# Revit family: Unterflurdose UGD250-3 für GES9_55
name_source: partatom
category: Generic Models
revit_build: Autodesk Revit 2015 (Build: 20140606_1530(x64)
units: mm (PartAtom-declared; Revit-internal decimal feet)

## types (1)
- UGD 250-3 9R
    "A" Dimension = 367 mm  [stored 1.20407 ft]
    "B" Dimension = 367 mm  [stored 1.20407 ft]
    Article Type = UGD55 250-3 9R
    Cover size "a" = 244 mm  [stored 0.800525 ft]
    Cover size "b" = 283 mm  [stored 0.928478 ft]
    GTIN = 4012195678724
    Height = 70 mm  [stored 0.229659 ft]
    HeightCalc = 70 mm  [stored 0.229659 ft]
    Manufacturer = OBO Bettermann
    Manufacturer Art. No. = 7410060
    Material = Steel, Galvanized
    Size "a" = 262 mm  [stored 0.85958 ft]
    URL = http://www.obo-bettermann.com
    Width = 200 mm  [stored 0.656168 ft]

note: [stored X ft] marks values corroborated as IEEE doubles in the binary element streams (Revit-internal decimal feet)

## geometry (parser evidence)
native form markers: Sweep x2
no freeform markers — native parametric forms only
